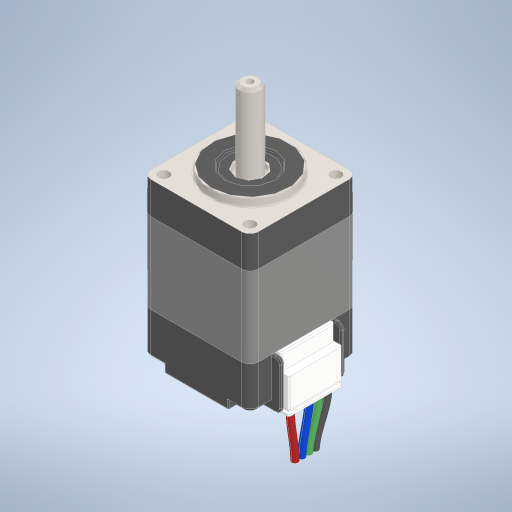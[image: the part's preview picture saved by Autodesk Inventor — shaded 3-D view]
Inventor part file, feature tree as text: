
AUTODESK INVENTOR PART (.ipt)
format: ipt  version: 2024.1 (Build 281209000, 209)  size: 1,186,816 bytes
history: native  units: in
note: dims shown in document units (in); Inventor stores cm internally (conversion verified against a paired STEP export)
features: extrude x1, sketch x1, pattern_circular x1
ambient origin geometry x8: Origin, YZ Plane, XZ Plane, XY Plane, X Axis, Y Axis, Z Axis, Center Point
bodies: Solid1 (feature_tree)
feature tree (3):
  extrude  "Extrusion1"  [1 undecoded]
  sketch  "Sketch1"  dims[d0=0.0in d1=0.0in]
  pattern_circular  "CirPattern1"
note: 1 required parameter value undecoded (feature->parameter linkage not recoverable at this tier; creation-order binding heuristic only, values carry confidence <= 0.55)
